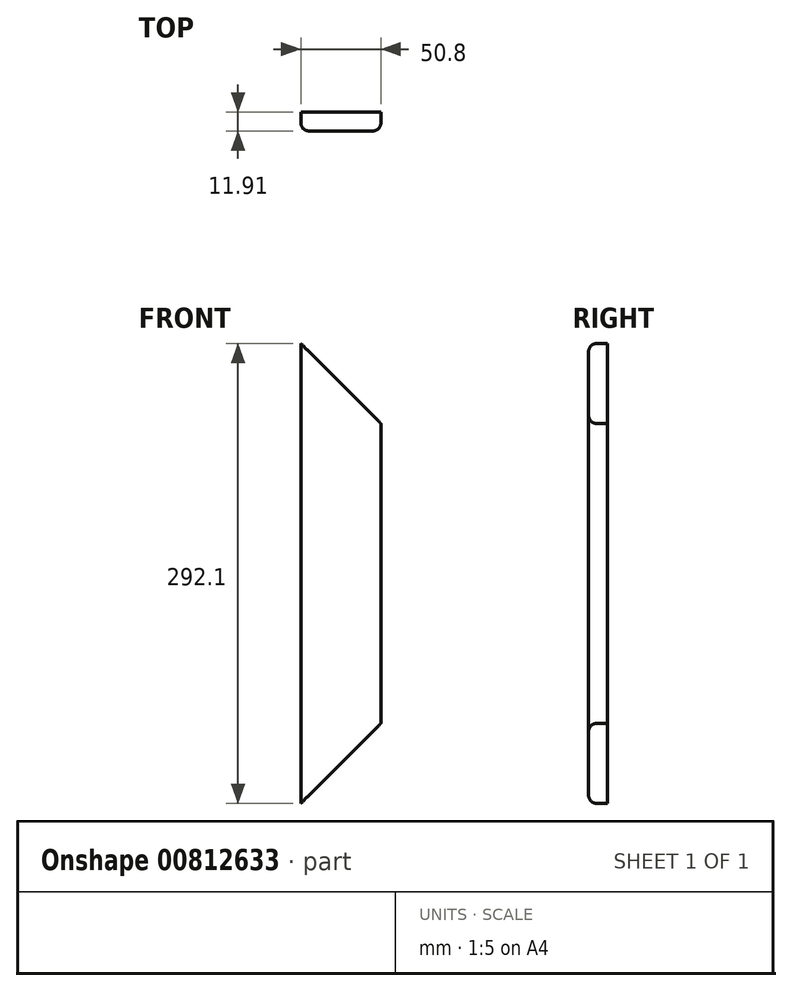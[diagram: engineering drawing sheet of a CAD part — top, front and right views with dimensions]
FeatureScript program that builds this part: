
annotation { "Feature Type Name" : "Feature", "Feature Type Description" : "" }
export const myFeature = defineFeature(function(context is Context, id is Id, definition is map)
    precondition{}
    {
        {
            var Q0;
            Q0=qCreatedBy(makeId("Front.planeOp"),FACE);
            var sketch = newSketch(context, id + "F0", { "sketchPlane" : qUnion([Q0])});
            skLineSegment(sketch, "E0", {"start": v(-59.36, 63.49) * mm, "end": v(-59.36, 38.09) * mm});
            skLineSegment(sketch, "E1", {"start": v(-59.36, 38.09) * mm, "end": v(-33.96, 38.09) * mm});
            skLineSegment(sketch, "E2", {"start": v(-33.96, 38.09) * mm, "end": v(-59.36, 63.49) * mm});
            skSolve(sketch);
        }
        {
            var Q0;
            Q0=qCreatedBy(makeId("Front.planeOp"),FACE);
            var sketch = newSketch(context, id + "F1", { "sketchPlane" : qUnion([Q0])});
            skLineSegment(sketch, "E3", {"start": v(-25.4, 146.05) * mm, "end": v(-25.4, -146.05) * mm});
            skLineSegment(sketch, "E4", {"start": v(-25.4, -146.05) * mm, "end": v(25.4, -95.25) * mm});
            skLineSegment(sketch, "E5", {"start": v(25.4, -95.25) * mm, "end": v(25.4, 95.25) * mm});
            skLineSegment(sketch, "E6", {"start": v(25.4, 95.25) * mm, "end": v(-25.4, 146.05) * mm});
            skSolve(sketch);
        }
        {
            var Q0;
            Q0=qSketchRegion(id+"F1",true);
            extrude(context, id + "F2", {"entities" : qUnion([Q0]), "depth" : 11.9 * mm, "offsetDistance" : 25.4 * mm});
        }
        {
            var Q0;
            Q0=makeQuery(id+"F2.opExtrude","CAP_EDGE",EDGE,{"disambiguationData":[OSD([sQuery(id+"F1.wireOp",EDGE,"E5")])],"isStart":false});
            fillet(context, id + "F3", {"entities" : qUnion([Q0]), "radius" : 5.08 * mm, "tangentPropagation" : true, "allowEdgeOverflow" : false});
        }
        {
            var Q0;
            Q0=makeQuery(id+"F2.opExtrude","CAP_EDGE",EDGE,{"disambiguationData":[OSD([sQuery(id+"F1.wireOp",EDGE,"E3")])],"isStart":false});
            fillet(context, id + "F4", {"entities" : qUnion([Q0]), "radius" : 5.08 * mm, "tangentPropagation" : true, "allowEdgeOverflow" : false});
        }
    });
